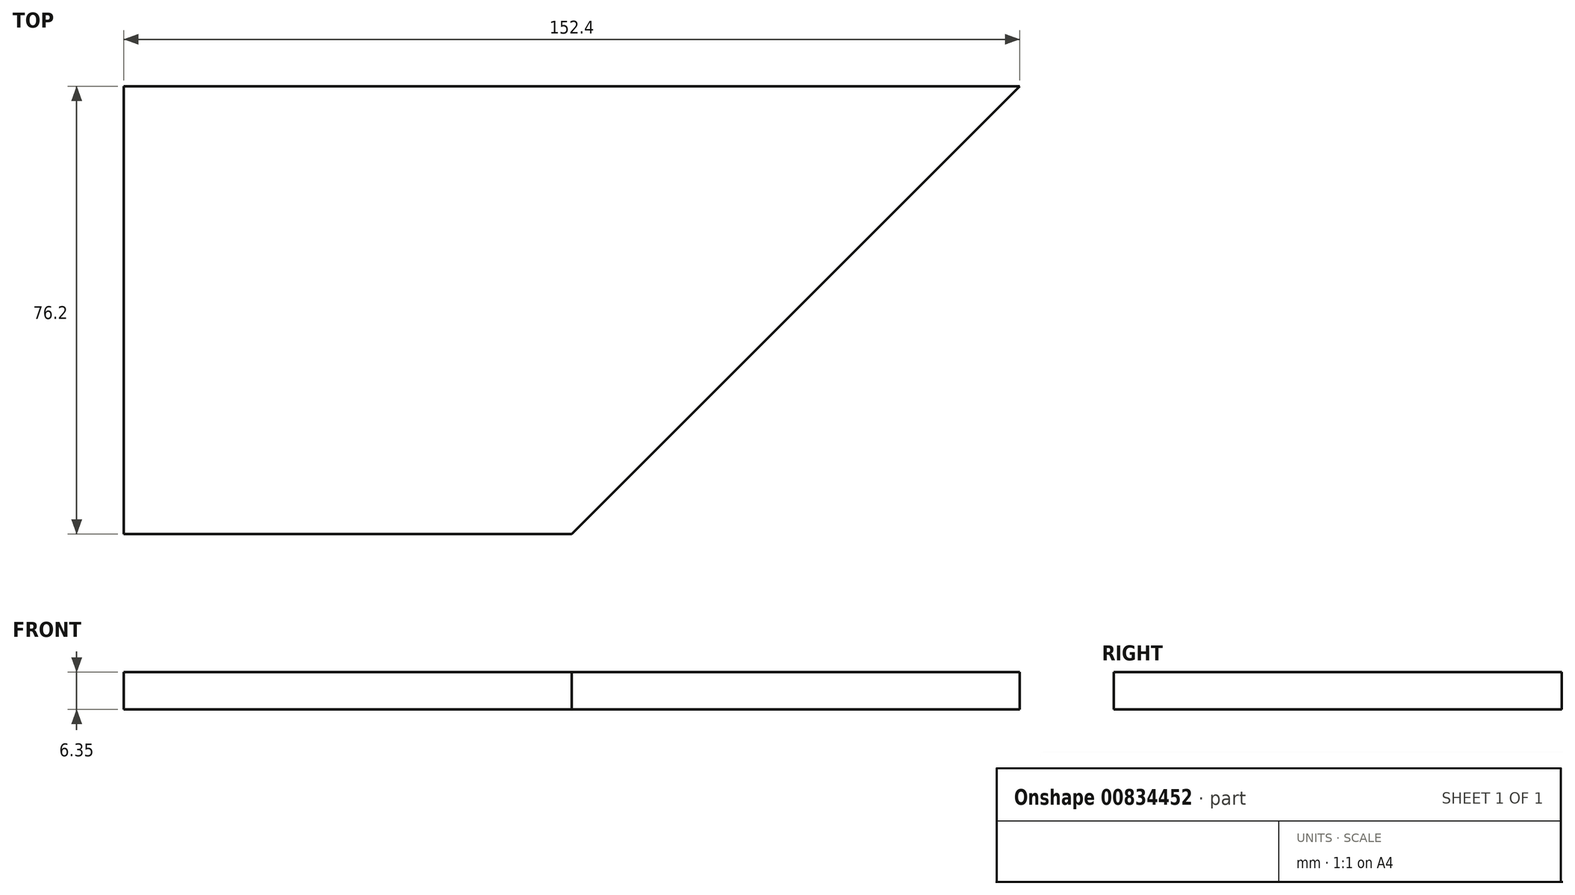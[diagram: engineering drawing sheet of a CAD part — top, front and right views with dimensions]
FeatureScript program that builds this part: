
annotation { "Feature Type Name" : "Feature", "Feature Type Description" : "" }
export const myFeature = defineFeature(function(context is Context, id is Id, definition is map)
    precondition{}
    {
        {
            var Q0;
            Q0=qCreatedBy(makeId("Top.planeOp"),FACE);
            var sketch = newSketch(context, id + "F0", { "sketchPlane" : qUnion([Q0])});
            skLineSegment(sketch, "E0.bottom", {"start": v(0, 0) * mm, "end": v(152.4, 0) * mm});
            skLineSegment(sketch, "E0.top", {"start": v(0, 76.2) * mm, "end": v(152.4, 76.2) * mm});
            skLineSegment(sketch, "E0.left", {"start": v(0, 0) * mm, "end": v(0, 76.2) * mm});
            skLineSegment(sketch, "E0.right", {"start": v(152.4, 0) * mm, "end": v(152.4, 76.2) * mm});
            skLineSegment(sketch, "E1", {"start": v(76.2, 0) * mm, "end": v(152.4, 76.2) * mm});
            skSolve(sketch);
        }
        {
            var Q0;
            {var subQ0=sQuery(id+"F0.wireOp",EDGE,"E0.right");Q0=makeQuery(id+"F0.imprint","IMPRINT",FACE,{"disambiguationData":[TD([[makeQuery(id+"F0.imprint","IMPRINT",EDGE,{"derivedFrom":subQ0}),1.0]])]});}
            var sketch = newSketch(context, id + "F1", { "sketchPlane" : qUnion([Q0])});
            skSolve(sketch);
        }
        {
            var Q0;
            Q0 = qSketchRegion(id + "F1", true);
            var Q1;
            Q1=makeQuery(id+"F0.imprint","IMPRINT",FACE,{"disambiguationData":[TD([[makeQuery(id+"F0.imprint","IMPRINT",EDGE,{"derivedFrom":sQuery(id+"F0.wireOp",EDGE,"E0.top")}),-1.0]])]});
            extrude(context, id + "F2", {"entities" : qUnion([Q0, Q1]), "depth" : 6.35 * mm, "offsetDistance" : 25.4 * mm});
        }
    });
